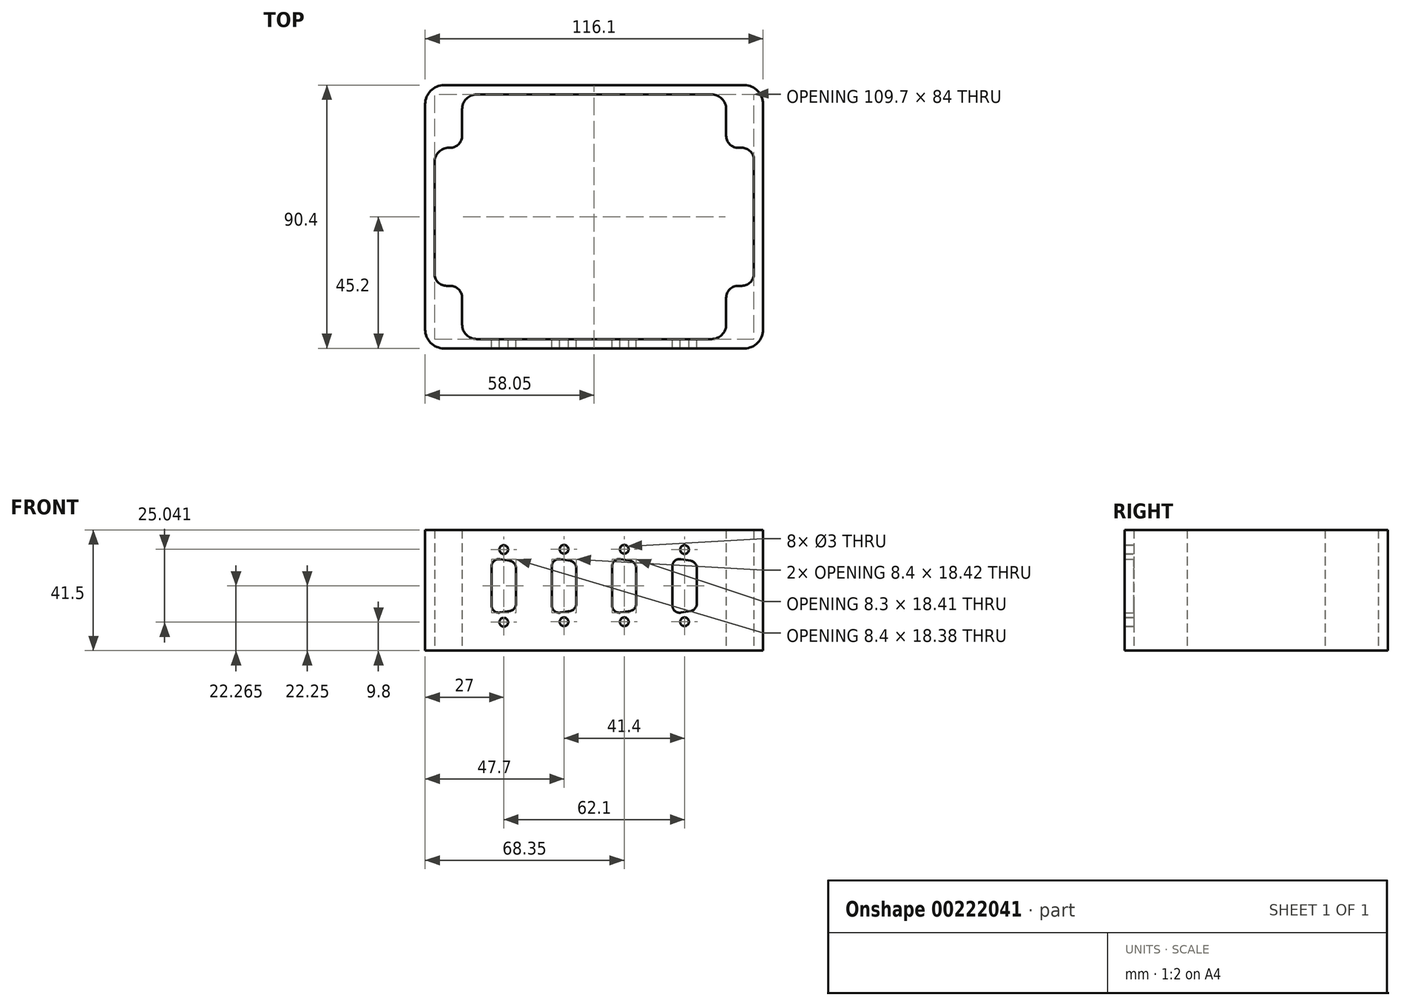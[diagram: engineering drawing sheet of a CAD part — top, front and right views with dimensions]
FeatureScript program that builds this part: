
annotation { "Feature Type Name" : "Feature", "Feature Type Description" : "" }
export const myFeature = defineFeature(function(context is Context, id is Id, definition is map)
    precondition{}
    {
        {
            var Q0;
            Q0=qCreatedBy(makeId("Top.planeOp"),FACE);
            var sketch = newSketch(context, id + "F0", { "sketchPlane" : qUnion([Q0])});
            skLineSegment(sketch, "E0.bottom", {"start": v(-51.4, 45.2) * mm, "end": v(51.7, 45.2) * mm});
            skLineSegment(sketch, "E0.top", {"start": v(-51.4, -45.2) * mm, "end": v(51.7, -45.2) * mm});
            skLineSegment(sketch, "E0.left", {"start": v(-57.9, 38.7) * mm, "end": v(-57.9, -38.7) * mm});
            skLineSegment(sketch, "E0.right", {"start": v(58.2, 38.7) * mm, "end": v(58.2, -38.7) * mm});
            skPoint(sketch, "E1.visualSharp", {"position": v(-57.9, 45.2) * mm});
            skArc(sketch, "E1.filletArc", {"start": v(-51.4, 45.2) * mm, "mid": v(-56, 43.3) * mm, "end": v(-57.9, 38.7) * mm});
            skPoint(sketch, "E2.visualSharp", {"position": v(58.2, 45.2) * mm});
            skArc(sketch, "E2.filletArc", {"start": v(58.2, 38.7) * mm, "mid": v(56.3, 43.3) * mm, "end": v(51.7, 45.2) * mm});
            skPoint(sketch, "E3.visualSharp", {"position": v(58.2, -45.2) * mm});
            skArc(sketch, "E3.filletArc", {"start": v(51.7, -45.2) * mm, "mid": v(56.3, -43.3) * mm, "end": v(58.2, -38.7) * mm});
            skPoint(sketch, "E4.visualSharp", {"position": v(-57.9, -45.2) * mm});
            skArc(sketch, "E4.filletArc", {"start": v(-57.9, -38.7) * mm, "mid": v(-56, -43.3) * mm, "end": v(-51.4, -45.2) * mm});
            skLineSegment(sketch, "E5.1", {"start": v(-54.7, 18.7) * mm, "end": v(-54.7, -19.54) * mm});
            skLineSegment(sketch, "E5.2", {"start": v(-40.2, 42) * mm, "end": v(40.5, 42) * mm});
            skLineSegment(sketch, "E5.5", {"start": v(55, 19.54) * mm, "end": v(55, -19.54) * mm});
            skLineSegment(sketch, "E5.7", {"start": v(-40.2, -42) * mm, "end": v(40.5, -42) * mm});
            skLineSegment(sketch, "E6.0", {"start": v(-45.2, 37) * mm, "end": v(-45.2, 27.86) * mm});
            skLineSegment(sketch, "E7.0", {"start": v(45.5, 37) * mm, "end": v(45.5, 27.86) * mm});
            skArc(sketch, "E8.filletArc", {"start": v(-40.2, 42) * mm, "mid": v(-43.74, 40.54) * mm, "end": v(-45.2, 37) * mm});
            skArc(sketch, "E9.filletArc", {"start": v(-45.2, -37) * mm, "mid": v(-43.74, -40.54) * mm, "end": v(-40.2, -42) * mm});
            skArc(sketch, "E10.filletArc", {"start": v(40.5, -42) * mm, "mid": v(44.04, -40.54) * mm, "end": v(45.5, -37) * mm});
            skArc(sketch, "E11.filletArc", {"start": v(45.5, 37) * mm, "mid": v(44.04, 40.54) * mm, "end": v(40.5, 42) * mm});
            skLineSegment(sketch, "E12.0", {"start": v(-49.7, 23.7) * mm, "end": v(-49.36, 23.7) * mm});
            skArc(sketch, "E13.filletArc", {"start": v(-49.7, 23.7) * mm, "mid": v(-53.24, 22.24) * mm, "end": v(-54.7, 18.7) * mm});
            skArc(sketch, "E14.filletArc", {"start": v(55, 19.54) * mm, "mid": v(53.78, 22.48) * mm, "end": v(50.84, 23.7) * mm});
            skLineSegment(sketch, "E15.0", {"start": v(-50.54, -23.7) * mm, "end": v(-49.36, -23.7) * mm});
            skArc(sketch, "E16.filletArc", {"start": v(-54.7, -19.54) * mm, "mid": v(-53.48, -22.48) * mm, "end": v(-50.54, -23.7) * mm});
            skArc(sketch, "E17.filletArc", {"start": v(50.84, -23.7) * mm, "mid": v(53.78, -22.48) * mm, "end": v(55, -19.54) * mm});
            skLineSegment(sketch, "E18.trimOffspring", {"start": v(49.66, 23.7) * mm, "end": v(50.84, 23.7) * mm});
            skLineSegment(sketch, "E19.trimOffspring", {"start": v(49.66, -23.7) * mm, "end": v(50.84, -23.7) * mm});
            skLineSegment(sketch, "E20.trimOffspring", {"start": v(-45.2, -27.86) * mm, "end": v(-45.2, -37) * mm});
            skLineSegment(sketch, "E21.trimOffspring", {"start": v(45.5, -27.86) * mm, "end": v(45.5, -37) * mm});
            skArc(sketch, "E22.filletArc", {"start": v(-49.36, 23.7) * mm, "mid": v(-46.42, 24.92) * mm, "end": v(-45.2, 27.86) * mm});
            skArc(sketch, "E23.filletArc", {"start": v(45.5, 27.86) * mm, "mid": v(46.72, 24.92) * mm, "end": v(49.66, 23.7) * mm});
            skArc(sketch, "E24.filletArc", {"start": v(-45.2, -27.86) * mm, "mid": v(-46.42, -24.92) * mm, "end": v(-49.36, -23.7) * mm});
            skArc(sketch, "E25.filletArc", {"start": v(49.66, -23.7) * mm, "mid": v(46.72, -24.92) * mm, "end": v(45.5, -27.86) * mm});
            skSolve(sketch);
        }
        {
            var Q0;
            Q0 = qSketchRegion(id + "F0", true);
            extrude(context, id + "F1", {"entities" : qUnion([Q0]), "depth" : 41.5 * mm});
        }
        {
            var Q0;
            Q0=qCreatedBy(makeId("Front.planeOp"),FACE);
            var sketch = newSketch(context, id + "F2", { "sketchPlane" : qUnion([Q0])});
            skLineSegment(sketch, "E26.0.0", {"start": v(-57.9, 0) * mm, "end": v(-51.4, 0) * mm});
            skLineSegment(sketch, "E26.0.1", {"start": v(-51.4, 0) * mm, "end": v(-51.4, 3) * mm});
            skLineSegment(sketch, "E27.0", {"start": v(-26.6, 6.8) * mm, "end": v(-35.2, 6.8) * mm, "construction": true});
            skLineSegment(sketch, "E28.0", {"start": v(35.5, 37.7) * mm, "end": v(26.9, 37.7) * mm, "construction": true});
            skLineSegment(sketch, "E29.0", {"start": v(-37.2, 8.8) * mm, "end": v(-37.2, 35.73) * mm, "construction": true});
            skLineSegment(sketch, "E30.0", {"start": v(-24.6, 8.8) * mm, "end": v(-24.6, 35.73) * mm, "construction": true});
            skLineSegment(sketch, "E31.0", {"start": v(-16.5, 8.8) * mm, "end": v(-16.5, 35.7) * mm, "construction": true});
            skLineSegment(sketch, "E32.0", {"start": v(-3.9, 8.8) * mm, "end": v(-3.9, 35.7) * mm, "construction": true});
            skLineSegment(sketch, "E33.0", {"start": v(4.2, 8.8) * mm, "end": v(4.2, 35.7) * mm, "construction": true});
            skLineSegment(sketch, "E34.0", {"start": v(24.9, 8.8) * mm, "end": v(24.9, 35.7) * mm, "construction": true});
            skLineSegment(sketch, "E35.0", {"start": v(37.5, 8.8) * mm, "end": v(37.5, 35.7) * mm, "construction": true});
            skLineSegment(sketch, "E36.trimOffspring", {"start": v(-24.6, 37.7) * mm, "end": v(-37.2, 37.7) * mm, "construction": true});
            skLineSegment(sketch, "E37.trimOffspring", {"start": v(-5.9, 37.7) * mm, "end": v(-14.5, 37.7) * mm, "construction": true});
            skLineSegment(sketch, "E38.trimOffspring", {"start": v(14.8, 37.7) * mm, "end": v(6.2, 37.7) * mm, "construction": true});
            skLineSegment(sketch, "E39", {"start": v(-37.2, 37.7) * mm, "end": v(-24.6, 37.7) * mm});
            skLineSegment(sketch, "E40", {"start": v(-35.2, 37.73) * mm, "end": v(-26.6, 37.73) * mm});
            skArc(sketch, "E41.filletArc", {"start": v(-35.2, 37.73) * mm, "mid": v(-36.61, 37.14) * mm, "end": v(-37.2, 35.73) * mm, "construction": true});
            skArc(sketch, "E42.filletArc", {"start": v(-24.6, 35.73) * mm, "mid": v(-25.19, 37.14) * mm, "end": v(-26.6, 37.73) * mm, "construction": true});
            skArc(sketch, "E43.filletArc", {"start": v(-37.2, 8.8) * mm, "mid": v(-36.61, 7.39) * mm, "end": v(-35.2, 6.8) * mm, "construction": true});
            skArc(sketch, "E44.filletArc", {"start": v(-26.6, 6.8) * mm, "mid": v(-25.19, 7.39) * mm, "end": v(-24.6, 8.8) * mm, "construction": true});
            skLineSegment(sketch, "E45", {"start": v(-16.5, 37.7) * mm, "end": v(-3.9, 37.7) * mm});
            skLineSegment(sketch, "E46", {"start": v(4.2, 37.7) * mm, "end": v(16.8, 37.7) * mm});
            skLineSegment(sketch, "E47", {"start": v(24.9, 37.7) * mm, "end": v(37.5, 37.7) * mm});
            skArc(sketch, "E48.filletArc", {"start": v(-14.5, 37.7) * mm, "mid": v(-15.91, 37.11) * mm, "end": v(-16.5, 35.7) * mm, "construction": true});
            skArc(sketch, "E49.filletArc", {"start": v(-3.9, 35.7) * mm, "mid": v(-4.49, 37.11) * mm, "end": v(-5.9, 37.7) * mm, "construction": true});
            skArc(sketch, "E50.filletArc", {"start": v(6.2, 37.7) * mm, "mid": v(4.79, 37.11) * mm, "end": v(4.2, 35.7) * mm, "construction": true});
            skArc(sketch, "E51.filletArc", {"start": v(16.8, 35.7) * mm, "mid": v(16.21, 37.11) * mm, "end": v(14.8, 37.7) * mm, "construction": true});
            skArc(sketch, "E52.filletArc", {"start": v(26.9, 37.7) * mm, "mid": v(25.49, 37.11) * mm, "end": v(24.9, 35.7) * mm, "construction": true});
            skArc(sketch, "E53.filletArc", {"start": v(37.5, 35.7) * mm, "mid": v(36.91, 37.11) * mm, "end": v(35.5, 37.7) * mm, "construction": true});
            skLineSegment(sketch, "E54", {"start": v(-14.5, 6.8) * mm, "end": v(-5.9, 6.8) * mm, "construction": true});
            skLineSegment(sketch, "E55.trimOffspring", {"start": v(6.2, 6.8) * mm, "end": v(14.8, 6.8) * mm, "construction": true});
            skLineSegment(sketch, "E56.trimOffspring", {"start": v(26.9, 6.8) * mm, "end": v(35.5, 6.8) * mm, "construction": true});
            skArc(sketch, "E57.filletArc", {"start": v(-16.5, 8.8) * mm, "mid": v(-15.91, 7.39) * mm, "end": v(-14.5, 6.8) * mm, "construction": true});
            skArc(sketch, "E58.filletArc", {"start": v(-5.9, 6.8) * mm, "mid": v(-4.49, 7.39) * mm, "end": v(-3.9, 8.8) * mm, "construction": true});
            skArc(sketch, "E59.filletArc", {"start": v(4.2, 8.8) * mm, "mid": v(4.79, 7.39) * mm, "end": v(6.2, 6.8) * mm, "construction": true});
            skArc(sketch, "E60.filletArc", {"start": v(14.8, 6.8) * mm, "mid": v(16.21, 7.39) * mm, "end": v(16.8, 8.8) * mm, "construction": true});
            skArc(sketch, "E61.filletArc", {"start": v(24.9, 8.8) * mm, "mid": v(25.49, 7.39) * mm, "end": v(26.9, 6.8) * mm, "construction": true});
            skArc(sketch, "E62.filletArc", {"start": v(35.5, 6.8) * mm, "mid": v(36.91, 7.39) * mm, "end": v(37.5, 8.8) * mm, "construction": true});
            skCircle(sketch, "E63", {"center": v(-30.9, 34.73) * mm, "radius": 1.5 * mm});
            skCircle(sketch, "E64", {"center": v(-30.9, 9.8) * mm, "radius": 1.5 * mm});
            skLineSegment(sketch, "E65", {"start": v(-30.9, 34.73) * mm, "end": v(41.34, 34.73) * mm});
            skCircle(sketch, "E66", {"center": v(-10.2, 34.84) * mm, "radius": 1.5 * mm});
            skCircle(sketch, "E67", {"center": v(10.5, 34.84) * mm, "radius": 1.5 * mm});
            skCircle(sketch, "E68", {"center": v(31.2, 34.73) * mm, "radius": 1.5 * mm});
            skCircle(sketch, "E69", {"center": v(31.2, 9.94) * mm, "radius": 1.5 * mm});
            skCircle(sketch, "E70", {"center": v(10.5, 9.94) * mm, "radius": 1.5 * mm});
            skCircle(sketch, "E71", {"center": v(-10.2, 9.94) * mm, "radius": 1.5 * mm});
            skLineSegment(sketch, "E72.0", {"start": v(-35.1, 15.56) * mm, "end": v(-35.1, 28.94) * mm});
            skLineSegment(sketch, "E73.0", {"start": v(-26.7, 16.1) * mm, "end": v(-26.7, 28.4) * mm});
            skLineSegment(sketch, "E74", {"start": v(-32.2, 31.41) * mm, "end": v(-28.8, 30.86) * mm});
            skLineSegment(sketch, "E75", {"start": v(-32.2, 13.09) * mm, "end": v(-28.8, 13.64) * mm});
            skArc(sketch, "E76.filletArc", {"start": v(-26.7, 28.4) * mm, "mid": v(-27.3, 30) * mm, "end": v(-28.8, 30.86) * mm});
            skArc(sketch, "E77.filletArc", {"start": v(-28.8, 13.64) * mm, "mid": v(-27.3, 14.5) * mm, "end": v(-26.7, 16.1) * mm});
            skArc(sketch, "E78.filletArc", {"start": v(-35.1, 15.56) * mm, "mid": v(-34.22, 13.65) * mm, "end": v(-32.2, 13.09) * mm});
            skArc(sketch, "E79.filletArc", {"start": v(-32.2, 31.41) * mm, "mid": v(-34.22, 30.85) * mm, "end": v(-35.1, 28.94) * mm});
            skLineSegment(sketch, "E80.0", {"start": v(-14.4, 15.55) * mm, "end": v(-14.4, 28.98) * mm});
            skLineSegment(sketch, "E81.0", {"start": v(-6, 16.12) * mm, "end": v(-6, 28.41) * mm});
            skLineSegment(sketch, "E82.0", {"start": v(6.3, 15.56) * mm, "end": v(6.3, 28.97) * mm});
            skLineSegment(sketch, "E83.0", {"start": v(16.7, 8.8) * mm, "end": v(16.7, 35.7) * mm, "construction": true});
            skLineSegment(sketch, "E84.0", {"start": v(14.6, 16.11) * mm, "end": v(14.6, 28.42) * mm});
            skLineSegment(sketch, "E85.0", {"start": v(27, 15.55) * mm, "end": v(27, 28.98) * mm});
            skLineSegment(sketch, "E86.0", {"start": v(35.4, 16.12) * mm, "end": v(35.4, 28.41) * mm});
            skLineSegment(sketch, "E87", {"start": v(-11.49, 31.44) * mm, "end": v(-8.09, 30.88) * mm});
            skLineSegment(sketch, "E88", {"start": v(9.22, 31.44) * mm, "end": v(12.52, 30.88) * mm});
            skLineSegment(sketch, "E89", {"start": v(29.91, 31.44) * mm, "end": v(33.31, 30.88) * mm});
            skLineSegment(sketch, "E90", {"start": v(29.91, 13.09) * mm, "end": v(33.31, 13.65) * mm});
            skLineSegment(sketch, "E91", {"start": v(9.22, 13.1) * mm, "end": v(12.52, 13.65) * mm});
            skLineSegment(sketch, "E92", {"start": v(-11.49, 13.09) * mm, "end": v(-8.09, 13.65) * mm});
            skArc(sketch, "E93.filletArc", {"start": v(-11.49, 31.44) * mm, "mid": v(-13.52, 30.89) * mm, "end": v(-14.4, 28.98) * mm});
            skArc(sketch, "E94.filletArc", {"start": v(-6, 28.41) * mm, "mid": v(-6.6, 30.03) * mm, "end": v(-8.09, 30.88) * mm});
            skArc(sketch, "E95.filletArc", {"start": v(-8.09, 13.65) * mm, "mid": v(-6.6, 14.5) * mm, "end": v(-6, 16.12) * mm});
            skArc(sketch, "E96.filletArc", {"start": v(-14.4, 15.55) * mm, "mid": v(-13.52, 13.64) * mm, "end": v(-11.49, 13.09) * mm});
            skArc(sketch, "E97.filletArc", {"start": v(9.22, 31.44) * mm, "mid": v(7.19, 30.88) * mm, "end": v(6.3, 28.97) * mm});
            skArc(sketch, "E98.filletArc", {"start": v(14.6, 28.42) * mm, "mid": v(14, 30.03) * mm, "end": v(12.52, 30.88) * mm});
            skArc(sketch, "E99.filletArc", {"start": v(12.52, 13.65) * mm, "mid": v(14, 14.5) * mm, "end": v(14.6, 16.11) * mm});
            skArc(sketch, "E100.filletArc", {"start": v(6.3, 15.56) * mm, "mid": v(7.19, 13.65) * mm, "end": v(9.22, 13.1) * mm});
            skArc(sketch, "E101.filletArc", {"start": v(29.91, 31.44) * mm, "mid": v(27.88, 30.89) * mm, "end": v(27, 28.98) * mm});
            skArc(sketch, "E102.filletArc", {"start": v(35.4, 28.41) * mm, "mid": v(34.8, 30.03) * mm, "end": v(33.31, 30.88) * mm});
            skArc(sketch, "E103.filletArc", {"start": v(33.31, 13.65) * mm, "mid": v(34.8, 14.5) * mm, "end": v(35.4, 16.12) * mm});
            skArc(sketch, "E104.filletArc", {"start": v(27, 15.55) * mm, "mid": v(27.88, 13.64) * mm, "end": v(29.91, 13.09) * mm});
            skSolve(sketch);
        }
        {
            var Q0;
            Q0 = qSketchRegion(id + "F2", true);
            extrude(context, id + "F3", {"entities" : qUnion([Q0]), "operationType" : NewBodyOperationType.REMOVE, "depth" : 103 * mm});
        }
    });
